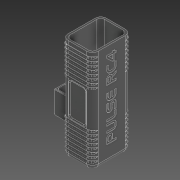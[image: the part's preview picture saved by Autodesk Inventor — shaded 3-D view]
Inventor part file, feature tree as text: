
AUTODESK INVENTOR PART (.ipt)
format: ipt  version: 2021 (Build 250183000, 183)  size: 2,069,504 bytes
history: native  units: mm
features: extrude x24, sketch x23, fillet x17, projected_geometry x10, plane x7, mirror x7, other x1
ambient origin geometry x8: Origin, YZ Plane, XZ Plane, XY Plane, X Axis, Y Axis, Z Axis, Center Point
bodies: Body1 (feature_tree)
feature tree (89):
  other  "Sólido1"
  extrude  "Extrusión1"  Depth=36.5mm
  extrude  "Extrusión2"  Depth=2.0mm
  extrude  "Extrusión3"  Depth=4.0mm
  plane  "Plano de trabajo1"
  mirror  "Simetría1"
  fillet  "Empalme1"  Radius=108.0mm
  plane  "Plano de trabajo2"
  extrude  "Extrusión4"  Depth=2.0mm
  plane  "Plano de trabajo3"
  mirror  "Simetría2"
  plane  "Plano de trabajo4"
  mirror  "Simetría3"
  plane  "Plano de trabajo5"
  mirror  "Simetría4"
  plane  "Plano de trabajo6"
  mirror  "Simetría5"
  plane  "Plano de trabajo8"
  mirror  "Simetría6"
  fillet  "Empalme2"  Radius=2.0mm
  fillet  "Empalme3"  Radius=2.0mm
  sketch  "Boceto4"  dims[d4=4.0mm d5=4.0mm d6=108.0mm d7=0.0mm]
  extrude  "Extrusión5"  Depth=2.0mm TaperAngle=0.0deg
  extrude  "Extrusión6"  Depth=6.0mm
  extrude  "Extrusión7"  Depth=11.0mm
  extrude  "Extrusión8"  [1 undecoded]
  extrude  "Extrusión9"  Depth=5.0mm
  extrude  "Extrusión10"  [1 undecoded]
  extrude  "Extrusión11"  [1 undecoded]
  extrude  "Extrusión12"  Depth=1.0mm
  extrude  "Extrusión13"  Depth=0.6mm TaperAngle=0.0deg
  extrude  "Extrusión14"  Depth=9.0mm
  extrude  "Extrusión15"  Depth=14.0mm TaperAngle=0.0deg
  extrude  "Extrusión16"  Depth=7.0mm
  fillet  "Empalme10"  Radius=1.8mm
  extrude  "Extrusión17"  Depth=2.0mm
  fillet  "Empalme13"  Radius=7.0mm
  fillet  "Empalme16"  Radius=6.0mm
  extrude  "Extrusión18"  Depth=8.0mm TaperAngle=0.0deg
  extrude  "Extrusión19"  Depth=10.0mm TaperAngle=0.0deg
  fillet  "Empalme20"  Radius=75.0mm
  fillet  "Empalme21"  Radius=75.0mm
  fillet  "Empalme22"  Radius=16.5mm
  fillet  "Empalme23"  Radius=11.273282mm
  fillet  "Empalme24"  Radius=5.0mm
  fillet  "Empalme25"  Radius=9.0mm
  fillet  "Empalme31"  Radius=9.0mm
  fillet  "Empalme32"  Radius=10.0mm
  extrude  "Extrusión20"  Depth=4.0mm
  fillet  "Empalme33"  Radius=6.0mm
  extrude  "Extrusión21"  Depth=2.0mm
  extrude  "Extrusión22"  Depth=2.0mm
  extrude  "Extrusión23"  Depth=0.5mm
  extrude  "Extrusión24"  Depth=0.5mm
  fillet  "Empalme34"  Radius=12.0mm
  fillet  "Empalme35"  Radius=1.5mm
  mirror  "Simetría8"
  sketch  "Boceto2"  dims[d0=27.85mm d1=36.5mm]
  sketch  "Boceto3"  dims[d2=2.0mm d3=6.0mm]
  sketch  "Boceto5"  dims[d8=2.0mm d9=0.0mm d10=8.0mm d11=2.0mm d12=2.0mm]
  sketch  "Boceto6"  dims[d13=2.0mm d14=2.0mm d15=0.0mm]
  sketch  "Boceto7"  dims[d16=20.0mm d17=6.0mm]
  sketch  "Boceto8"  dims[d18=3.2mm d19=11.0mm]
  projected_geometry  "Contorno proyectado1"
  sketch  "Boceto9"  dims[d20=5.0mm d21=-4.0mm]
  sketch  "Boceto10"  dims[d22=0.8mm d23=5.0mm]
  sketch  "Boceto11"  dims[d24=2.0mm d25=0.0mm d26=-3.0mm]
  sketch  "Boceto12"  dims[d27=-4.0mm d28=-8.0mm]
  sketch  "Boceto13"  dims[d29=-33.5mm d30=1.0mm]
  projected_geometry  "Contorno proyectado2"
  sketch  "Boceto14"  dims[d31=1.0mm d32=0.6mm d33=0.0mm]
  sketch  "Boceto18"  dims[d37=20.0mm d39=9.0mm]
  sketch  "Boceto19"  dims[d40=24.0mm d41=14.0mm d42=0.0mm]
  projected_geometry  "Contorno proyectado7"
  sketch  "Boceto20"  dims[d43=8.0mm d44=0.0mm d45=7.0mm d46=1.8mm]
  sketch  "Boceto21"  dims[d47=15.0mm d48=0.0mm d49=2.0mm d50=7.0mm d51=0.0mm d53=6.0mm d54=0.0mm]
  sketch  "Boceto22"  dims[d56=14.0mm d57=0.0mm d58=8.0mm d59=0.0mm]
  sketch  "Boceto24"  dims[d60=8.0mm d61=0.0mm d63=8.0mm d64=0.0mm d65=75.0mm d66=75.0mm d67=16.5mm d68=11.273282mm d70=5.0mm d72=9.0mm d73=9.0mm d75=10.0mm d76=0.0mm]
  projected_geometry  "Contorno proyectado9"
  sketch  "Boceto25"  dims[d78=6.0mm d79=4.0mm d80=6.0mm]
  sketch  "Boceto26"  dims[d81=2.0mm d82=2.0mm]
  projected_geometry  "Contorno proyectado10"
  projected_geometry  "Contorno proyectado11"
  sketch  "Boceto27"  dims[d83=0.5mm d84=0.0mm d85=2.0mm]
  projected_geometry  "Contorno proyectado12"
  projected_geometry  "Contorno proyectado13"
  sketch  "Boceto28"  dims[d88=0.5mm d89=0.0mm d90=1.5mm d93=4.0mm d96=12.0mm d97=1.5mm d98=1.653837mm d99=10.0mm d100=0.0mm d101=10.0mm d102=0.0mm d104=1.5mm d105=1.5mm d106=1.5mm d107=1.5mm d108=0.5mm d109=0.5mm d115=1.0mm d116=5.0mm d117=1.0mm d118=10.0mm d119=0.0mm d120=0.2mm d122=16.9mm d123=10.0mm d124=0.0mm d125=10.0mm d126=0.0mm d127=9.0mm d128=0.0mm d129=9.0mm d130=0.0mm d131=2.0mm d132=2.0mm d74=0.5mm d77=0.872665mm]
  projected_geometry  "Contorno proyectado14"
  projected_geometry  "Contorno proyectado15"
note: 3 required parameter values undecoded (feature->parameter linkage not recoverable at this tier; creation-order binding heuristic only, values carry confidence <= 0.55)
